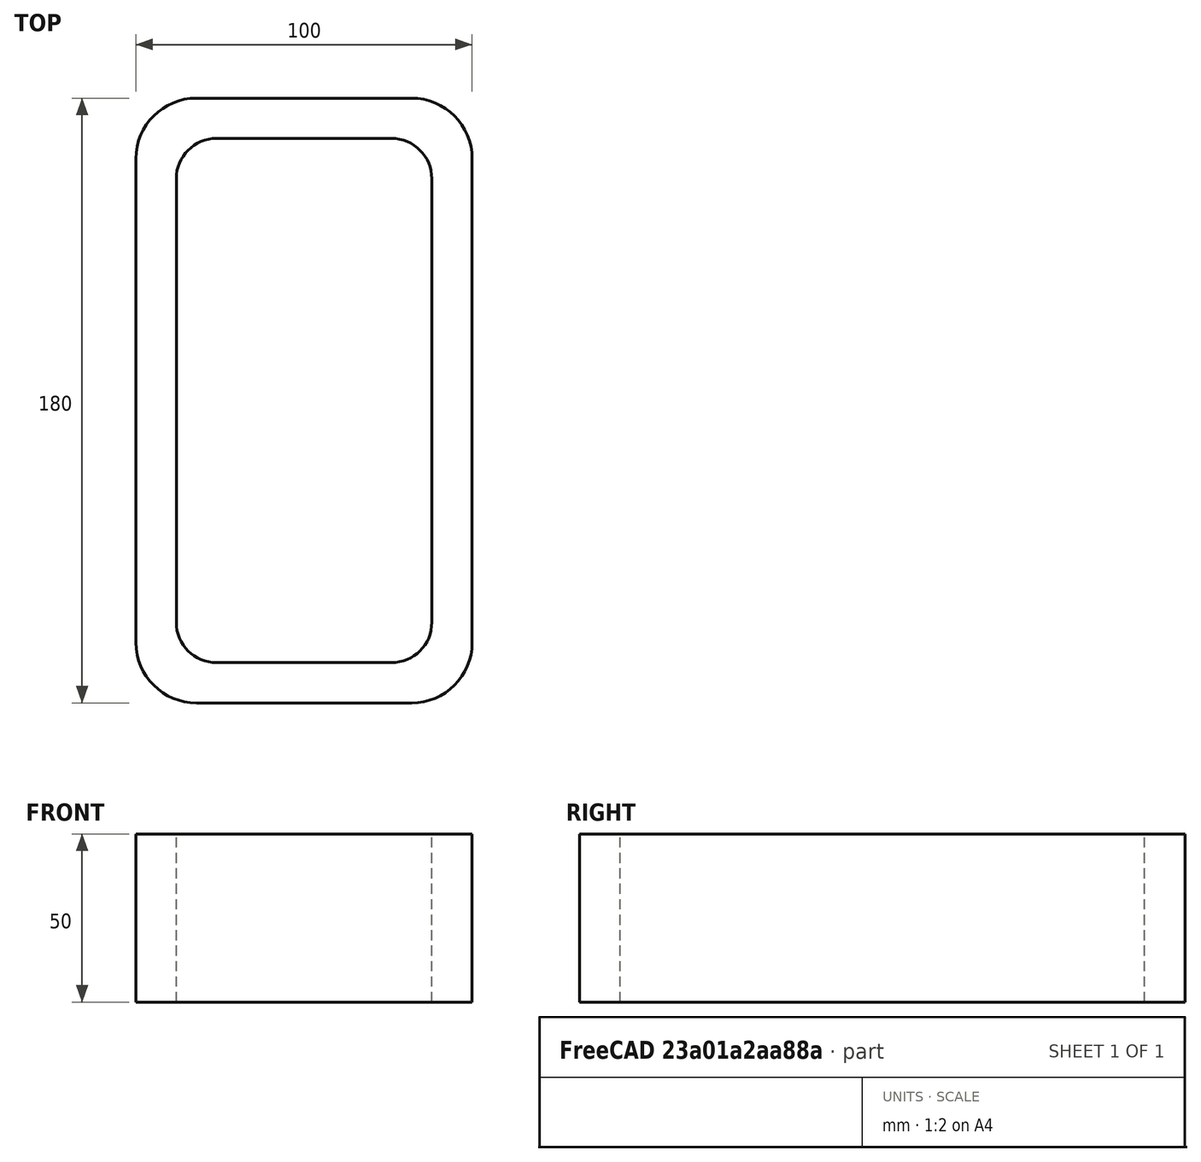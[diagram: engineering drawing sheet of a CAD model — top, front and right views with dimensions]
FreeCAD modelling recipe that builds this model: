
FCSTD DOCUMENT  (FreeCAD 0.15R4671 (Git))
Label: Rectangular hollow section 180x100x12 EN10219 S235JRH
License: All rights reserved
LicenseURL: http://en.wikipedia.org/wiki/All_rights_reserved
objects: Sketcher::SketchObject×1, Part::Extrusion×1
note: 2 computed .brp shape members not serialized (recipe doc carries the construction recipe); baked Part::Feature solids carry a one-line shape summary decoded from their .brp

FEATURE [Sketcher::SketchObject] Sketch
  sketch-geometry (16):
    g0: LineSegment StartX=-26 StartY=78 StartZ=0 EndX=26 EndY=78 EndZ=0
    g1: LineSegment StartX=38 StartY=66 StartZ=0 EndX=38 EndY=-66 EndZ=0
    g2: LineSegment StartX=26 StartY=-78 StartZ=0 EndX=-26 EndY=-78 EndZ=0
    g3: LineSegment StartX=-38 StartY=-66 StartZ=0 EndX=-38 EndY=66 EndZ=0
    g4: LineSegment StartX=-32 StartY=90 StartZ=0 EndX=32 EndY=90 EndZ=0
    g5: LineSegment StartX=50 StartY=72 StartZ=0 EndX=50 EndY=-72 EndZ=0
    g6: LineSegment StartX=32 StartY=-90 StartZ=0 EndX=-32 EndY=-90 EndZ=0
    g7: LineSegment StartX=-50 StartY=-72 StartZ=0 EndX=-50 EndY=72 EndZ=0
    g8: ArcOfCircle CenterX=-26 CenterY=66 CenterZ=0 NormalX=0 NormalY=0 NormalZ=1 Radius=12 StartAngle=1.5708 EndAngle=3.14159
    g9: ArcOfCircle CenterX=26 CenterY=66 CenterZ=0 NormalX=0 NormalY=0 NormalZ=1 Radius=12 StartAngle=0 EndAngle=1.5708
    g10: ArcOfCircle CenterX=26 CenterY=-66 CenterZ=0 NormalX=0 NormalY=0 NormalZ=1 Radius=12 StartAngle=4.71239 EndAngle=6.28319
    g11: ArcOfCircle CenterX=-26 CenterY=-66 CenterZ=0 NormalX=0 NormalY=0 NormalZ=1 Radius=12 StartAngle=3.14159 EndAngle=4.71239
    g12: ArcOfCircle CenterX=32 CenterY=72 CenterZ=0 NormalX=0 NormalY=0 NormalZ=1 Radius=18 StartAngle=0 EndAngle=1.5708
    g13: ArcOfCircle CenterX=32 CenterY=-72 CenterZ=0 NormalX=0 NormalY=0 NormalZ=1 Radius=18 StartAngle=4.71239 EndAngle=6.28319
    g14: ArcOfCircle CenterX=-32 CenterY=-72 CenterZ=0 NormalX=0 NormalY=0 NormalZ=1 Radius=18 StartAngle=3.14159 EndAngle=4.71239
    g15: ArcOfCircle CenterX=-32 CenterY=72 CenterZ=0 NormalX=0 NormalY=0 NormalZ=1 Radius=18 StartAngle=1.5708 EndAngle=3.14159
  constraints (36):
    c: Horizontal(g2)
    c: Vertical(g3)
    c: Horizontal(g6)
    c: Vertical(g7)
    c: Tangent(g3,g8) = 1.5708
    c: Tangent(g0,g8) = 1.5708
    c: Tangent(g0,g9) = 1.5708
    c: Tangent(g1,g9) = 1.5708
    c: Tangent(g1,g10) = 1.5708
    c: Tangent(g2,g10) = 1.5708
    c: Tangent(g2,g11) = 1.5708
    c: Tangent(g3,g11) = 1.5708
    c: Tangent(g4,g12) = 1.5708
    c: Tangent(g5,g12) = 1.5708
    c: Tangent(g5,g13) = 1.5708
    c: Tangent(g6,g13) = 1.5708
    c: Tangent(g6,g14) = 1.5708
    c: Tangent(g7,g14) = 1.5708
    c: Tangent(g7,g15) = 1.5708
    c: Tangent(g4,g15) = 1.5708
    c: Equal(g9,g8)
    c: Equal(g9,g11)
    c: Equal(g9,g10)
    c: Equal(g12,g15)
    c: Equal(g12,g14)
    c: Equal(g12,g13)
    c: Symmetric(g4,g6,g-1)
    c: Symmetric(g7,g5,g-2)
    c: DistanceY(g4,g6) = -180
    c: DistanceX(g7,g5) = 100
    c: Symmetric(g3,g1,g-2)
    c: Symmetric(g0,g2,g-1)
    c: DistanceY(g0,g4) = 12
    c: DistanceX(g5,g1) = -12
    c: Radius(g9) = 12
    c: Radius(g12) = 18
FEATURE [Part::Extrusion] Extrude  label="Rectangular hollow section 180x100x12 EN10219 S235JRH"
  Base = -> Sketch
  Dir = (0,0,50)
  Solid = true
